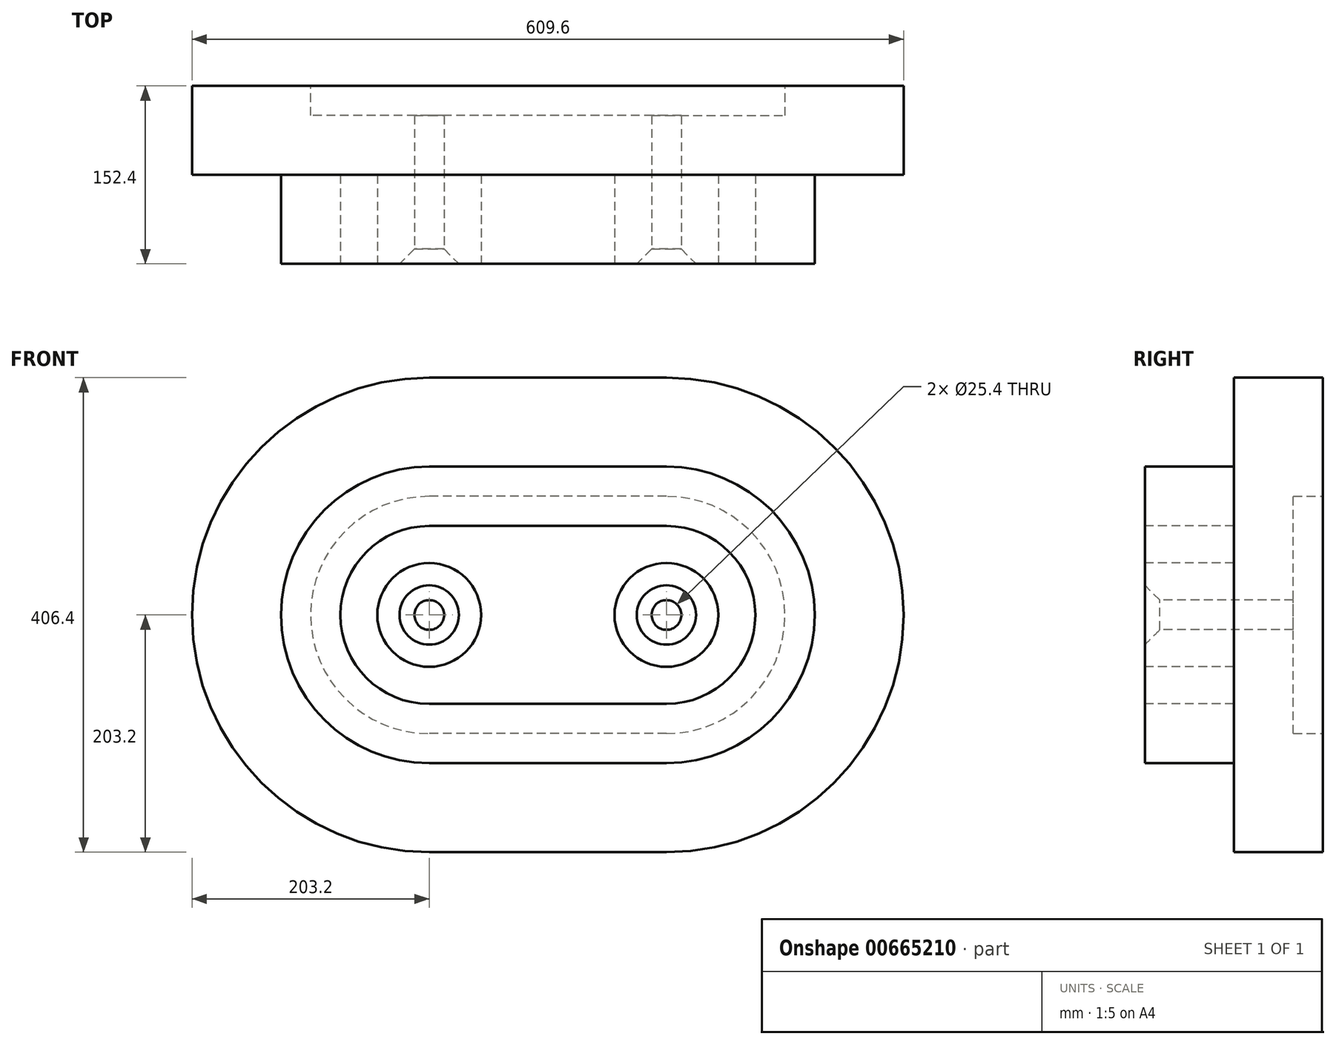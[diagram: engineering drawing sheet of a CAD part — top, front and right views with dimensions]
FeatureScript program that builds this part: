
annotation { "Feature Type Name" : "Feature", "Feature Type Description" : "" }
export const myFeature = defineFeature(function(context is Context, id is Id, definition is map)
    precondition{}
    {
        {
            var Q0;
            Q0=qCreatedBy(makeId("Front.planeOp"),FACE);
            var sketch = newSketch(context, id + "F0", { "sketchPlane" : qUnion([Q0])});
            skArc(sketch, "E0", {"start": v(0, 203.2) * mm, "mid": v(-203.2, 0) * mm, "end": v(0, -203.2) * mm});
            skArc(sketch, "E1", {"start": v(203.2, -203.2) * mm, "mid": v(406.4, 0) * mm, "end": v(203.2, 203.2) * mm});
            skLineSegment(sketch, "E2", {"start": v(0, -203.2) * mm, "end": v(203.2, -203.2) * mm});
            skLineSegment(sketch, "E3", {"start": v(0, 203.2) * mm, "end": v(203.2, 203.2) * mm});
            skArc(sketch, "E4", {"start": v(0, 127) * mm, "mid": v(-127, 0) * mm, "end": v(0, -127) * mm});
            skArc(sketch, "E5", {"start": v(203.2, -127) * mm, "mid": v(330.2, 0) * mm, "end": v(203.2, 127) * mm});
            skLineSegment(sketch, "E6", {"start": v(0, 127) * mm, "end": v(203.2, 127) * mm});
            skLineSegment(sketch, "E7", {"start": v(0, -127) * mm, "end": v(203.2, -127) * mm});
            skSolve(sketch);
        }
        {
            var Q0;
            Q0 = qSketchRegion(id + "F0", true);
            var Q1;
            Q1=makeQuery(id+"F0.imprint","IMPRINT",FACE,{"disambiguationData":[TD([[makeQuery(id+"F0.imprint","IMPRINT",EDGE,{"derivedFrom":sQuery(id+"F0.wireOp",EDGE,"E4")}),1.0]])]});
            extrude(context, id + "F1", {"entities" : qUnion([Q0, Q1]), "depth" : 76.2 * mm, "offsetDistance" : 25.4 * mm});
        }
        {
            var Q0;
            Q0=makeQuery(id+"F0.imprint","IMPRINT",FACE,{"disambiguationData":[TD([[makeQuery(id+"F0.imprint","IMPRINT",EDGE,{"derivedFrom":sQuery(id+"F0.wireOp",EDGE,"E4")}),1.0]])]});
            extrude(context, id + "F2", {"entities" : qUnion([Q0]), "operationType" : NewBodyOperationType.ADD, "depth" : 152.4 * mm, "offsetDistance" : 25.4 * mm});
        }
        {
            var Q0;
            Q0=makeQuery(id+"F2.opExtrude","CAP_FACE",FACE,{"disambiguationData":[OSD([sQuery(id+"F0.wireOp",EDGE,"E4"),sQuery(id+"F0.wireOp",EDGE,"E5"),sQuery(id+"F0.wireOp",EDGE,"E6"),sQuery(id+"F0.wireOp",EDGE,"E7")])],"isStart":false});
            var sketch = newSketch(context, id + "F3", { "sketchPlane" : qUnion([Q0])});
            skArc(sketch, "E8", {"start": v(0, 76.2) * mm, "mid": v(-76.2, 0) * mm, "end": v(0, -76.2) * mm});
            skArc(sketch, "E9", {"start": v(203.2, -76.2) * mm, "mid": v(279.4, 0) * mm, "end": v(203.2, 76.2) * mm});
            skLineSegment(sketch, "E10", {"start": v(0, 76.2) * mm, "end": v(203.2, 76.2) * mm});
            skLineSegment(sketch, "E11", {"start": v(0, -76.2) * mm, "end": v(203.2, -76.2) * mm});
            skCircle(sketch, "E12", {"center": v(0, 0) * mm, "radius": 44.45 * mm});
            skCircle(sketch, "E13", {"center": v(203.2, 0) * mm, "radius": 44.45 * mm});
            skSolve(sketch);
        }
        {
            var Q0;
            Q0=makeQuery(id+"F3.imprint","IMPRINT",FACE,{"disambiguationData":[TD([[makeQuery(id+"F3.imprint","IMPRINT",EDGE,{"derivedFrom":sQuery(id+"F3.wireOp",EDGE,"E8")}),1.0]])]});
            extrude(context, id + "F4", {"entities" : qUnion([Q0]), "operationType" : NewBodyOperationType.REMOVE, "oppositeDirection" : true, "depth" : 76.2 * mm, "offsetDistance" : 25.4 * mm});
        }
        {
            var Q0;
            Q0=makeQuery(id+"F4.boolean.opBoolean","SPLIT",FACE,{"disambiguationData":[TD([makeQuery(id+"F4.opExtrude","SWEPT_FACE",FACE,{"disambiguationData":[OSD([sQuery(id+"F3.wireOp",EDGE,"E12")])]})])],"derivedFrom":makeQuery(id+"F2.opExtrude","CAP_FACE",FACE,{"disambiguationData":[OSD([sQuery(id+"F0.wireOp",EDGE,"E4"),sQuery(id+"F0.wireOp",EDGE,"E5"),sQuery(id+"F0.wireOp",EDGE,"E6"),sQuery(id+"F0.wireOp",EDGE,"E7")])],"isStart":false})});
            var sketch = newSketch(context, id + "F5", { "sketchPlane" : qUnion([Q0])});
            skLineSegment(sketch, "E14", {"start": v(0, 0) * mm, "end": v(203.2, 0) * mm});
            skSolve(sketch);
        }
        {
            var Q0;
            Q0=sQuery(id+"F5.wireOp",VERTEX,"E14.start");
            var Q1;
            Q1=sQuery(id+"F5.wireOp",VERTEX,"E14.end");
            var Q2;
            Q2=makeQuery(id+"F1.opExtrude","SWEPT_BODY",BODY,{"disambiguationData":[OSD([sQuery(id+"F0.wireOp",EDGE,"E0"),sQuery(id+"F0.wireOp",EDGE,"E1"),sQuery(id+"F0.wireOp",EDGE,"E2"),sQuery(id+"F0.wireOp",EDGE,"E3")])]});
            hole(context, id + "F6", {"style" : HoleStyle.C_SINK, "endStyle" : HoleEndStyle.THROUGH, "holeDiameter" : 25.4 * mm, "cSinkDiameter" : 50.8 * mm, "cSinkAngle" : 90 * degree, "majorDiameter" : 6.35 * mm, "isTappedThrough" : true, "tappedDepth" : 12.7 * mm, "tapClearance" : 3, "locations" : qUnion([Q0, Q1]), "scope" : qUnion([Q2])});
        }
        {
            var Q0;
            Q0=makeQuery(id+"F0.imprint","IMPRINT",FACE,{"disambiguationData":[TD([[makeQuery(id+"F0.imprint","IMPRINT",EDGE,{"derivedFrom":sQuery(id+"F0.wireOp",EDGE,"E4")}),1.0]])]});
            var sketch = newSketch(context, id + "F7", { "sketchPlane" : qUnion([Q0])});
            skArc(sketch, "E15", {"start": v(0, 101.6) * mm, "mid": v(-101.6, 0) * mm, "end": v(0, -101.6) * mm});
            skArc(sketch, "E16", {"start": v(203.2, -101.6) * mm, "mid": v(304.8, 0) * mm, "end": v(203.2, 101.6) * mm});
            skLineSegment(sketch, "E17", {"start": v(203.2, 101.6) * mm, "end": v(0, 101.6) * mm});
            skLineSegment(sketch, "E18", {"start": v(203.2, -101.6) * mm, "end": v(0, -101.6) * mm});
            skSolve(sketch);
        }
        {
            var Q0;
            Q0=makeQuery(id+"F7.imprint","IMPRINT",FACE,{"disambiguationData":[TD([[makeQuery(id+"F7.imprint","IMPRINT",EDGE,{"derivedFrom":sQuery(id+"F7.wireOp",EDGE,"E15")}),1.0]])]});
            extrude(context, id + "F8", {"entities" : qUnion([Q0]), "operationType" : NewBodyOperationType.REMOVE, "depth" : 25.4 * mm, "offsetDistance" : 25.4 * mm});
        }
    });
